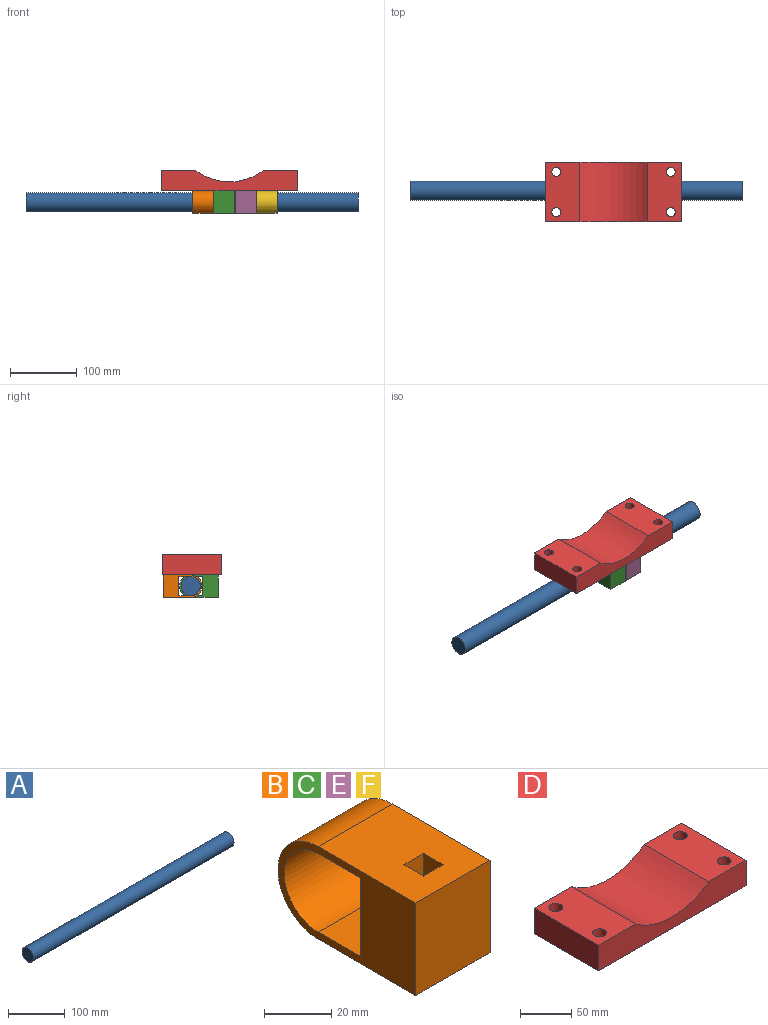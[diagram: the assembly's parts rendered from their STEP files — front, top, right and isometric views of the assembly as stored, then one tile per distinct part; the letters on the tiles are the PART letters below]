
ASSEMBLY  parts=6 mates=7
PART A: 3 faces, bbox 497.6x28.6x28.6 mm
  f0: cylinder r=14.29mm len=497.59mm, axis (1,0,0), area 44668.8mm2, adj f1,f2
  f1: plane 28.58x28.58mm, normal (-1,0,0), area 641.3mm2, adj f0
  f2: plane 28.58x28.58mm, normal (1,0,0), area 641.3mm2, adj f0
PART B: 14 faces, bbox 31.1x58x33.7 mm
  f0: plane 41.15x31.12mm, normal (0,0,-1), area 1212.2mm2, adj f5,f6,f8,f9,f10,f11,f12,f13
  f1: plane 41.15x31.12mm, normal (0,0,1), area 1212.2mm2, adj f5,f6,f8,f9,f10,f11,f12,f13
  f2: cylinder r=14.29mm len=31.12mm, axis (-1,0,0), area 1396.6mm2, adj f3,f7,f8,f9
  f3: plane 31.12x17.78mm, normal (0,0,-1), area 553.2mm2, adj f2,f4,f8,f9
  f4: plane 31.12x28.58mm, normal (0,1,0), area 889.1mm2, adj f3,f7,f8,f9
  f5: cylinder r=16.83mm len=33.66mm, axis (-1,0,0), area 1644.9mm2, adj f0,f1,f8,f9
  f6: plane 33.66x31.12mm, normal (0,-1,0), area 1047.2mm2, adj f0,f1,f8,f9
  f7: plane 31.12x17.78mm, normal (0,0,1), area 553.2mm2, adj f2,f4,f8,f9
  f8: plane 57.98x33.66mm, normal (1,0,0), area 1000.9mm2, adj f0,f1,f2,f3,f4,f5,f6,f7
  f9: plane 57.98x33.66mm, normal (-1,0,0), area 1000.9mm2, adj f0,f1,f2,f3,f4,f5,f6,f7
  f10: plane 33.66x8.26mm, normal (-1,0,0), area 277.8mm2, adj f0,f1,f11,f13
  f11: plane 33.66x8.26mm, normal (0,1,0), area 277.8mm2, adj f0,f1,f10,f12
  f12: plane 33.66x8.26mm, normal (1,0,0), area 277.8mm2, adj f0,f1,f11,f13
  f13: plane 33.66x8.26mm, normal (0,-1,0), area 277.8mm2, adj f0,f1,f10,f12
PART C: same geometry as B
PART D: 12 faces, bbox 203.2x88.9x30.5 mm
  f0: plane 88.9x51.12mm, normal (0,0,1), area 4259.7mm2, adj f1,f4,f6,f7,f8,f9
  f1: plane 203.2x30.48mm, normal (0,-1,0), area 5036.1mm2, adj f0,f2,f3,f5,f6,f7
  f2: plane 88.9x51.12mm, normal (0,0,1), area 4259.7mm2, adj f1,f4,f5,f7,f10,f11
  f3: plane 203.2x88.9mm, normal (0,0,-1), area 17495.1mm2, adj f1,f4,f5,f6,f8,f9,f10,f11
  f4: plane 203.2x30.48mm, normal (0,1,0), area 5036.1mm2, adj f0,f2,f3,f5,f6,f7
  f5: plane 88.9x30.48mm, normal (1,0,0), area 2709.7mm2, adj f1,f2,f3,f4
  f6: plane 88.9x30.48mm, normal (-1,0,0), area 2709.7mm2, adj f0,f1,f3,f4
  f7: cylinder r=84.14mm len=100.97mm, axis (0,-1,0), area 9626.5mm2, adj f0,f1,f2,f4
  f8: cylinder r=6.73mm len=30.48mm, axis (0,0,1), area 1289.1mm2, adj f0,f3
  f9: cylinder r=6.73mm len=30.48mm, axis (0,0,1), area 1289.1mm2, adj f0,f3
  f10: cylinder r=6.73mm len=30.48mm, axis (0,0,1), area 1289.1mm2, adj f2,f3
  f11: cylinder r=6.73mm len=30.48mm, axis (0,0,1), area 1289.1mm2, adj f2,f3
PART E: same geometry as B
PART F: same geometry as B
PLACE A t=(5.75,33.3,-38.99)mm fixed
PLACE B rot(axis=(1,0,0),180deg) t=(103.27,33.3,-67.56)mm
PLACE C t=(134.39,33.3,-38.99)mm
PLACE D t=(81.72,31.45,-38.99)mm
PLACE E t=(167.38,33.3,-38.99)mm
PLACE F rot(axis=(1,0,0),180deg) t=(198.49,33.3,-67.56)mm
MATE slider E.f2 <-> A.f0  axis (-1,0,0) through (121.78,33.3,-53.28)mm
MATE planar E.f8 <-> F.f9  axis (1,0,0) through (121.78,15.52,-53.28)mm
MATE planar D.f3 <-> E.f1  axis (0,0,-1) through (81.72,31.45,-36.45)mm
MATE slider B.f2 <-> A.f0  axis (-1,0,0) through (57.68,33.3,-53.28)mm
MATE slider F.f2 <-> A.f0  axis (-1,0,0) through (152.9,33.3,-53.28)mm
MATE slider C.f2 <-> A.f0  axis (-1,0,0) through (88.79,33.3,-53.28)mm
MATE planar B.f8 <-> C.f9  axis (1,0,0) through (57.68,56.02,-53.28)mm
